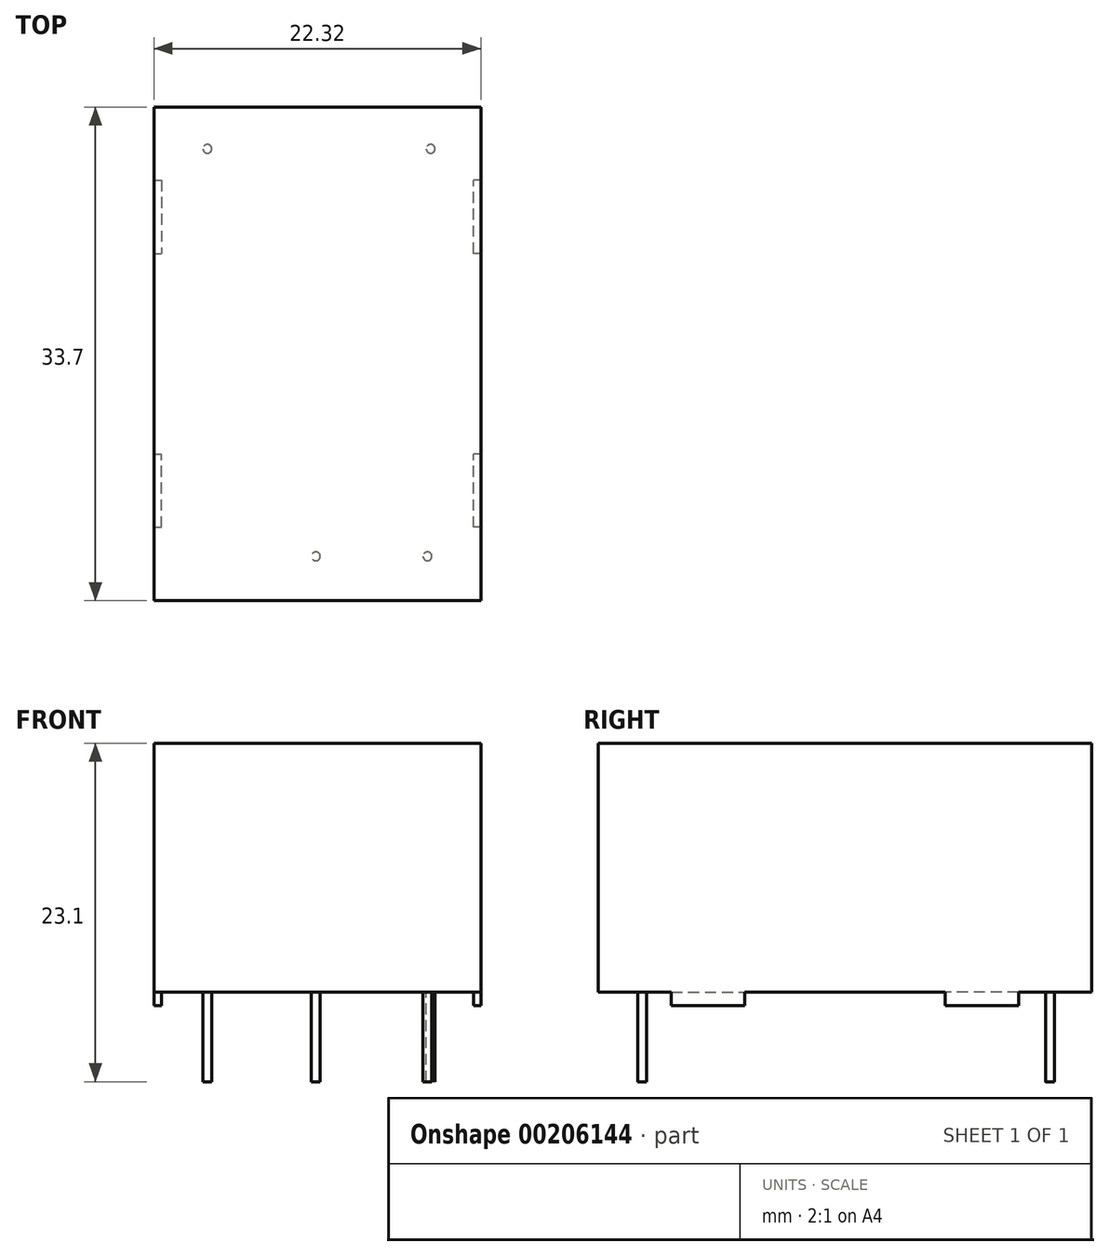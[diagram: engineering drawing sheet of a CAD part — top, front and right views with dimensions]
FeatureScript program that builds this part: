
annotation { "Feature Type Name" : "Feature", "Feature Type Description" : "" }
export const myFeature = defineFeature(function(context is Context, id is Id, definition is map)
    precondition{}
    {
        {
            var Q0;
            Q0=qCreatedBy(makeId("Top.planeOp"),FACE);
            var sketch = newSketch(context, id + "F0", { "sketchPlane" : qUnion([Q0])});
            skLineSegment(sketch, "E0.bottom", {"start": v(11.16, -16.85) * mm, "end": v(-11.16, -16.85) * mm});
            skLineSegment(sketch, "E0.top", {"start": v(11.16, 16.85) * mm, "end": v(-11.16, 16.85) * mm});
            skLineSegment(sketch, "E0.left", {"start": v(11.16, -16.85) * mm, "end": v(11.16, 16.85) * mm});
            skLineSegment(sketch, "E0.right", {"start": v(-11.16, -16.85) * mm, "end": v(-11.16, 16.85) * mm});
            skPoint(sketch, "E0.middle", {"position": v(0, 0) * mm});
            skSolve(sketch);
        }
        {
            var Q0;
            Q0=makeQuery(id+"F0.imprint","IMPRINT",FACE,{"disambiguationData":[TD([[makeQuery(id+"F0.imprint","IMPRINT",EDGE,{"derivedFrom":sQuery(id+"F0.wireOp",EDGE,"E0.bottom")}),-1.0]])]});
            extrude(context, id + "F1", {"entities" : qUnion([Q0]), "depth" : 17 * mm});
        }
        {
            var Q0;
            Q0=makeQuery(id+"F1.opExtrude","CAP_FACE",FACE,{"disambiguationData":[OSD([sQuery(id+"F0.wireOp",EDGE,"E0.bottom"),sQuery(id+"F0.wireOp",EDGE,"E0.top"),sQuery(id+"F0.wireOp",EDGE,"E0.left"),sQuery(id+"F0.wireOp",EDGE,"E0.right")])],"isStart":true});
            var sketch = newSketch(context, id + "F2", { "sketchPlane" : qUnion([Q0])});
            skCircle(sketch, "E1", {"center": v(-0.11, 13.83) * mm, "radius": 0.3 * mm});
            skCircle(sketch, "E2", {"center": v(7.5, 13.83) * mm, "radius": 0.3 * mm});
            skCircle(sketch, "E3", {"center": v(-7.5, -13.99) * mm, "radius": 0.3 * mm});
            skCircle(sketch, "E4", {"center": v(7.73, -14) * mm, "radius": 0.3 * mm});
            skLineSegment(sketch, "E5.bottom", {"start": v(11.16, 11.85) * mm, "end": v(10.66, 11.85) * mm});
            skLineSegment(sketch, "E5.top", {"start": v(11.16, 6.85) * mm, "end": v(10.66, 6.85) * mm});
            skLineSegment(sketch, "E5.left", {"start": v(11.16, 11.85) * mm, "end": v(11.16, 6.85) * mm});
            skLineSegment(sketch, "E5.right", {"start": v(10.66, 11.85) * mm, "end": v(10.66, 6.85) * mm});
            skLineSegment(sketch, "E6.bottom", {"start": v(11.16, -6.85) * mm, "end": v(10.66, -6.85) * mm});
            skLineSegment(sketch, "E6.top", {"start": v(11.16, -11.85) * mm, "end": v(10.66, -11.85) * mm});
            skLineSegment(sketch, "E6.left", {"start": v(11.16, -6.85) * mm, "end": v(11.16, -11.85) * mm});
            skLineSegment(sketch, "E6.right", {"start": v(10.66, -6.85) * mm, "end": v(10.66, -11.85) * mm});
            skLineSegment(sketch, "E7.bottom", {"start": v(-11.16, 11.85) * mm, "end": v(-10.66, 11.85) * mm});
            skLineSegment(sketch, "E7.top", {"start": v(-11.16, 6.85) * mm, "end": v(-10.66, 6.85) * mm});
            skLineSegment(sketch, "E7.left", {"start": v(-11.16, 11.85) * mm, "end": v(-11.16, 6.85) * mm});
            skLineSegment(sketch, "E7.right", {"start": v(-10.66, 11.85) * mm, "end": v(-10.66, 6.85) * mm});
            skPoint(sketch, "E8.oppositeSnap0", {"position": v(-10.66, 9.35) * mm});
            skLineSegment(sketch, "E8.bottom", {"start": v(-11.16, -11.85) * mm, "end": v(-10.66, -11.85) * mm});
            skLineSegment(sketch, "E8.top", {"start": v(-11.16, -6.85) * mm, "end": v(-10.66, -6.85) * mm});
            skLineSegment(sketch, "E8.left", {"start": v(-11.16, -11.85) * mm, "end": v(-11.16, -6.85) * mm});
            skLineSegment(sketch, "E8.right", {"start": v(-10.66, -11.85) * mm, "end": v(-10.66, -6.85) * mm});
            skSolve(sketch);
        }
        {
            var Q0;
            Q0=makeQuery(id+"F2.imprint","IMPRINT",FACE,{"disambiguationData":[TD([[makeQuery(id+"F2.imprint","IMPRINT",EDGE,{"derivedFrom":sQuery(id+"F2.wireOp",EDGE,"E1")}),1.0]])]});
            var Q1;
            Q1=makeQuery(id+"F2.imprint","IMPRINT",FACE,{"disambiguationData":[TD([[makeQuery(id+"F2.imprint","IMPRINT",EDGE,{"derivedFrom":sQuery(id+"F2.wireOp",EDGE,"E2")}),1.0]])]});
            var Q2;
            Q2=makeQuery(id+"F2.imprint","IMPRINT",FACE,{"disambiguationData":[TD([[makeQuery(id+"F2.imprint","IMPRINT",EDGE,{"derivedFrom":sQuery(id+"F2.wireOp",EDGE,"E3")}),1.0]])]});
            var Q3;
            Q3=makeQuery(id+"F2.imprint","IMPRINT",FACE,{"disambiguationData":[TD([[makeQuery(id+"F2.imprint","IMPRINT",EDGE,{"derivedFrom":sQuery(id+"F2.wireOp",EDGE,"E4")}),1.0]])]});
            extrude(context, id + "F3", {"entities" : qUnion([Q0, Q1, Q2, Q3]), "operationType" : NewBodyOperationType.ADD, "depth" : 6.1 * mm});
        }
        {
            var Q0;
            Q0=makeQuery(id+"F2.imprint","IMPRINT",FACE,{"disambiguationData":[TD([[makeQuery(id+"F2.imprint","IMPRINT",EDGE,{"derivedFrom":sQuery(id+"F2.wireOp",EDGE,"E7.bottom")}),-1.0]])]});
            var Q1;
            Q1=makeQuery(id+"F2.imprint","IMPRINT",FACE,{"disambiguationData":[TD([[makeQuery(id+"F2.imprint","IMPRINT",EDGE,{"derivedFrom":sQuery(id+"F2.wireOp",EDGE,"E5.bottom")}),1.0]])]});
            var Q2;
            Q2=makeQuery(id+"F2.imprint","IMPRINT",FACE,{"disambiguationData":[TD([[makeQuery(id+"F2.imprint","IMPRINT",EDGE,{"derivedFrom":sQuery(id+"F2.wireOp",EDGE,"E8.bottom")}),1.0]])]});
            var Q3;
            Q3=makeQuery(id+"F2.imprint","IMPRINT",FACE,{"disambiguationData":[TD([[makeQuery(id+"F2.imprint","IMPRINT",EDGE,{"derivedFrom":sQuery(id+"F2.wireOp",EDGE,"E6.bottom")}),1.0]])]});
            extrude(context, id + "F4", {"entities" : qUnion([Q0, Q1, Q2, Q3]), "operationType" : NewBodyOperationType.ADD, "depth" : 0.9 * mm});
        }
    });
